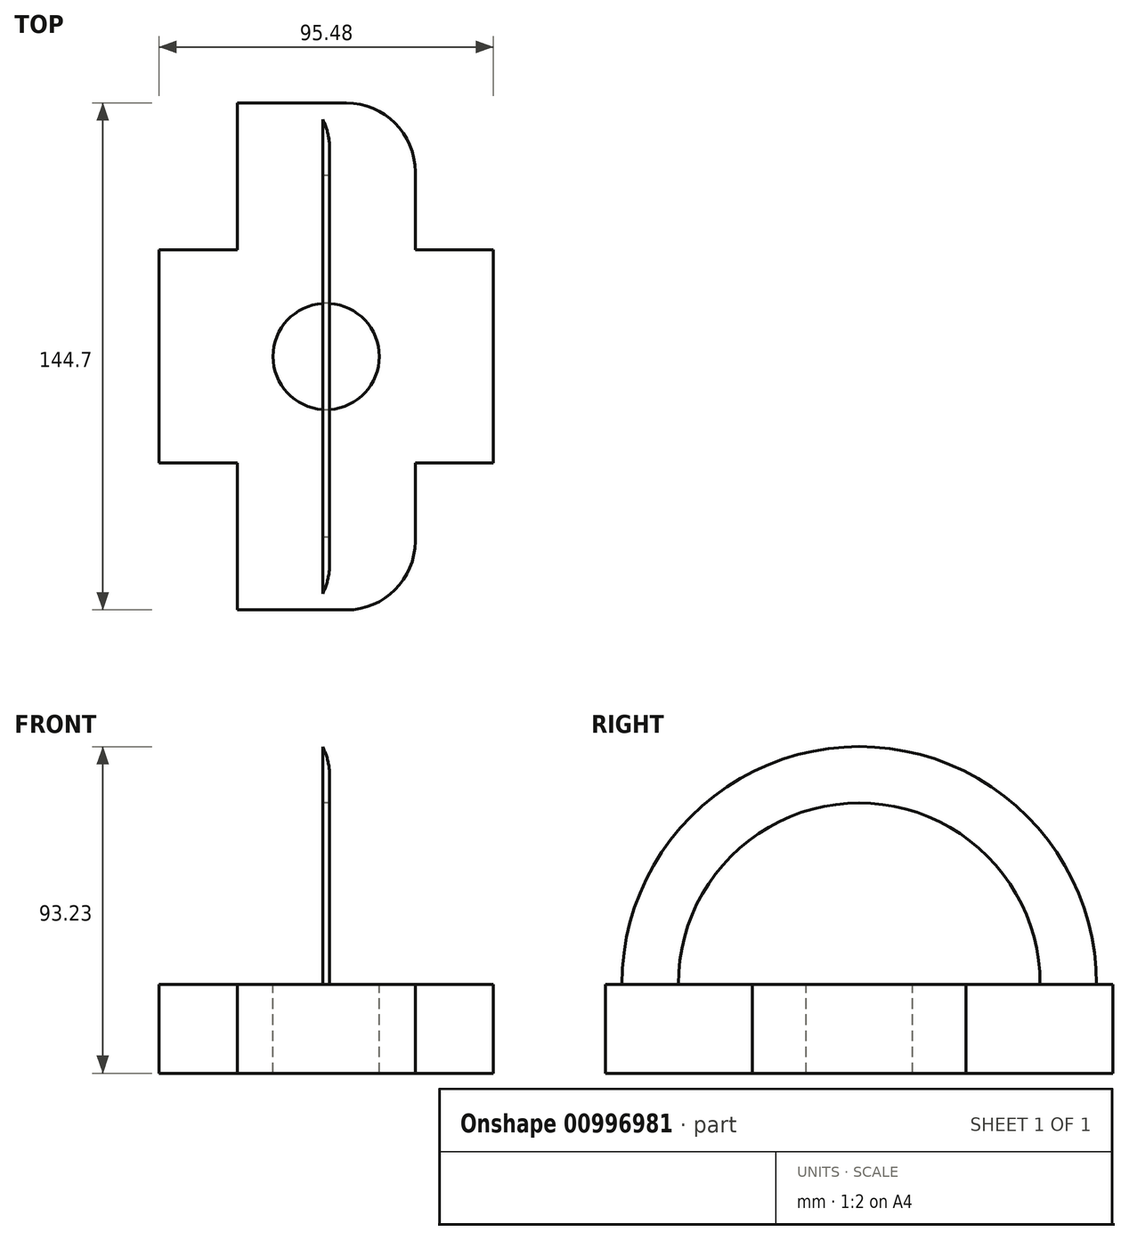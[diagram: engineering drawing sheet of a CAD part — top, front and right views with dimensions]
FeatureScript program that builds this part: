
annotation { "Feature Type Name" : "Feature", "Feature Type Description" : "" }
export const myFeature = defineFeature(function(context is Context, id is Id, definition is map)
    precondition{}
    {
        {
            assignVariable(context, id + "F0", {"name" : "hossz", "anyValue" : 2});
        }
        {
            var Q0;
            Q0=qCreatedBy(makeId("Top.planeOp"),FACE);
            var sketch = newSketch(context, id + "F1", { "sketchPlane" : qUnion([Q0])});
            skLineSegment(sketch, "E0.bottom", {"start": v(-47.74, 30.44) * mm, "end": v(47.74, 30.44) * mm});
            skLineSegment(sketch, "E0.top", {"start": v(-47.74, -30.44) * mm, "end": v(47.74, -30.44) * mm});
            skLineSegment(sketch, "E0.left", {"start": v(-47.74, 30.44) * mm, "end": v(-47.74, -30.44) * mm});
            skLineSegment(sketch, "E0.right", {"start": v(47.74, 30.44) * mm, "end": v(47.74, -30.44) * mm});
            skPoint(sketch, "E0.middle", {"position": v(0, 0) * mm});
            skLineSegment(sketch, "E1.bottom", {"start": v(-25.4, -72.35) * mm, "end": v(25.4, -72.35) * mm});
            skLineSegment(sketch, "E1.top", {"start": v(-25.4, 72.35) * mm, "end": v(25.4, 72.35) * mm});
            skLineSegment(sketch, "E1.left", {"start": v(-25.4, -72.35) * mm, "end": v(-25.4, 72.35) * mm});
            skLineSegment(sketch, "E1.right", {"start": v(25.4, -72.35) * mm, "end": v(25.4, 72.35) * mm});
            skSolve(sketch);
        }
        {
            var Q0;
            {var subQ0=sQuery(id+"F1.wireOp",EDGE,"E1.left");var subQ1=sQuery(id+"F1.wireOp",EDGE,"E0.bottom");var subQ2=makeQuery(id+"F1.imprint","INTERSECT",VERTEX,{"derivedFrom":[subQ1,subQ0]});Q0=makeQuery(id+"F1.imprint","IMPRINT",FACE,{"disambiguationData":[TD([[makeQuery(id+"F1.imprint","IMPRINT",EDGE,{"disambiguationData":[TD([[subQ2,-1.0]])],"derivedFrom":subQ1}),-1.0]])]});}
            var Q1;
            {var subQ0=sQuery(id+"F1.wireOp",EDGE,"E0.left");Q1=makeQuery(id+"F1.imprint","IMPRINT",FACE,{"disambiguationData":[TD([[makeQuery(id+"F1.imprint","IMPRINT",EDGE,{"derivedFrom":subQ0}),1.0]])]});}
            var Q2;
            {var subQ5=sQuery(id+"F1.wireOp",EDGE,"E1.top");Q2=makeQuery(id+"F1.imprint","IMPRINT",FACE,{"disambiguationData":[TD([[makeQuery(id+"F1.imprint","IMPRINT",EDGE,{"derivedFrom":subQ5}),-1.0]])]});}
            var Q3;
            {var subQ0=sQuery(id+"F1.wireOp",EDGE,"E0.right");Q3=makeQuery(id+"F1.imprint","IMPRINT",FACE,{"disambiguationData":[TD([[makeQuery(id+"F1.imprint","IMPRINT",EDGE,{"derivedFrom":subQ0}),-1.0]])]});}
            var Q4;
            {var subQ5=sQuery(id+"F1.wireOp",EDGE,"E1.bottom");Q4=makeQuery(id+"F1.imprint","IMPRINT",FACE,{"disambiguationData":[TD([[makeQuery(id+"F1.imprint","IMPRINT",EDGE,{"derivedFrom":subQ5}),1.0]])]});}
            extrude(context, id + "F2", {"entities" : qUnion([Q0, Q1, Q2, Q3, Q4]), "depth" : 25.4 * mm, "offsetDistance" : 25.4 * mm});
        }
        {
            var Q0;
            Q0=qCreatedBy(makeId("Right.planeOp"),FACE);
            var sketch = newSketch(context, id + "F3", { "sketchPlane" : qUnion([Q0])});
            skArc(sketch, "E2", {"start": v(67.69, 25.17) * mm, "mid": v(0, 93.23) * mm, "end": v(-67.69, 25.17) * mm});
            skArc(sketch, "E3", {"start": v(51.6, 25.17) * mm, "mid": v(0, 77.15) * mm, "end": v(-51.6, 25.17) * mm});
            skLineSegment(sketch, "E4", {"start": v(-67.69, 25.17) * mm, "end": v(67.69, 25.17) * mm});
            skSolve(sketch);
        }
        {
            var Q0;
            {var subQ0=sQuery(id+"F3.wireOp",EDGE,"E2");Q0=makeQuery(id+"F3.imprint","IMPRINT",FACE,{"disambiguationData":[TD([[makeQuery(id+"F3.imprint","IMPRINT",EDGE,{"derivedFrom":subQ0}),1.0]])]});}
            extrude(context, id + "F4", {"entities" : qUnion([Q0]), "operationType" : NewBodyOperationType.ADD, "endBound" : BoundingType.SYMMETRIC, "depth" : (getVariable(context, 'hossz')) * mm, "offsetDistance" : 25.4 * mm});
        }
        {
            var Q0;
            Q0=makeQuery(id+"F4.opExtrude","CAP_EDGE",EDGE,{"disambiguationData":[OSD([sQuery(id+"F3.wireOp",EDGE,"E2")])],"isStart":false});
            var Q1;
            Q1=makeQuery(id+"F2.opExtrude","SWEPT_EDGE",EDGE,{"disambiguationData":[OSD([sQuery(id+"F1.wireOp",EDGE,"E1.bottom"),sQuery(id+"F1.wireOp",EDGE,"E1.right")])]});
            var Q2;
            Q2=makeQuery(id+"F2.opExtrude","SWEPT_EDGE",EDGE,{"disambiguationData":[OSD([sQuery(id+"F1.wireOp",EDGE,"E1.top"),sQuery(id+"F1.wireOp",EDGE,"E1.right")])]});
            fillet(context, id + "F5", {"entities" : qUnion([Q0, Q1, Q2]), "radius" : 19.62 * mm, "tangentPropagation" : true, "allowEdgeOverflow" : false});
        }
        {
            var Q0;
            {var subQ0=sQuery(id+"F1.wireOp",EDGE,"E1.right");var subQ1=sQuery(id+"F1.wireOp",EDGE,"E1.top");var subQ2=sQuery(id+"F1.wireOp",EDGE,"E0.bottom");var subQ4=sQuery(id+"F1.wireOp",EDGE,"E1.bottom");var subQ5=sQuery(id+"F1.wireOp",EDGE,"E0.top");var subQ7=sQuery(id+"F1.wireOp",EDGE,"E1.left");var subQ9=sQuery(id+"F1.wireOp",EDGE,"E0.right");var subQ11=sQuery(id+"F1.wireOp",EDGE,"E0.left");Q0=makeQuery(id+"F4.boolean.opBoolean","SPLIT",FACE,{"disambiguationData":[TD([makeQuery(id+"F2.opExtrude","SWEPT_FACE",FACE,{"disambiguationData":[OSD([subQ11])]})])],"derivedFrom":makeQuery(id+"F2.opExtrude","CAP_FACE",FACE,{"disambiguationData":[OSD([subQ2,subQ5,subQ11,subQ9,subQ4,subQ1,subQ7,subQ0])],"isStart":false})});}
            var sketch = newSketch(context, id + "F6", { "sketchPlane" : qUnion([Q0])});
            skCircle(sketch, "E5", {"center": v(0, 0) * mm, "radius": 15.17 * mm});
            skSolve(sketch);
        }
        {
            var Q0;
            Q0=makeQuery(id+"F6.imprint","IMPRINT",FACE,{"disambiguationData":[TD([[makeQuery(id+"F6.imprint","IMPRINT",EDGE,{"derivedFrom":sQuery(id+"F6.wireOp",EDGE,"E5")}),1.0]])]});
            extrude(context, id + "F7", {"entities" : qUnion([Q0]), "operationType" : NewBodyOperationType.REMOVE, "oppositeDirection" : true, "depth" : 64.52 * mm, "offsetDistance" : 25.4 * mm});
        }
    });
